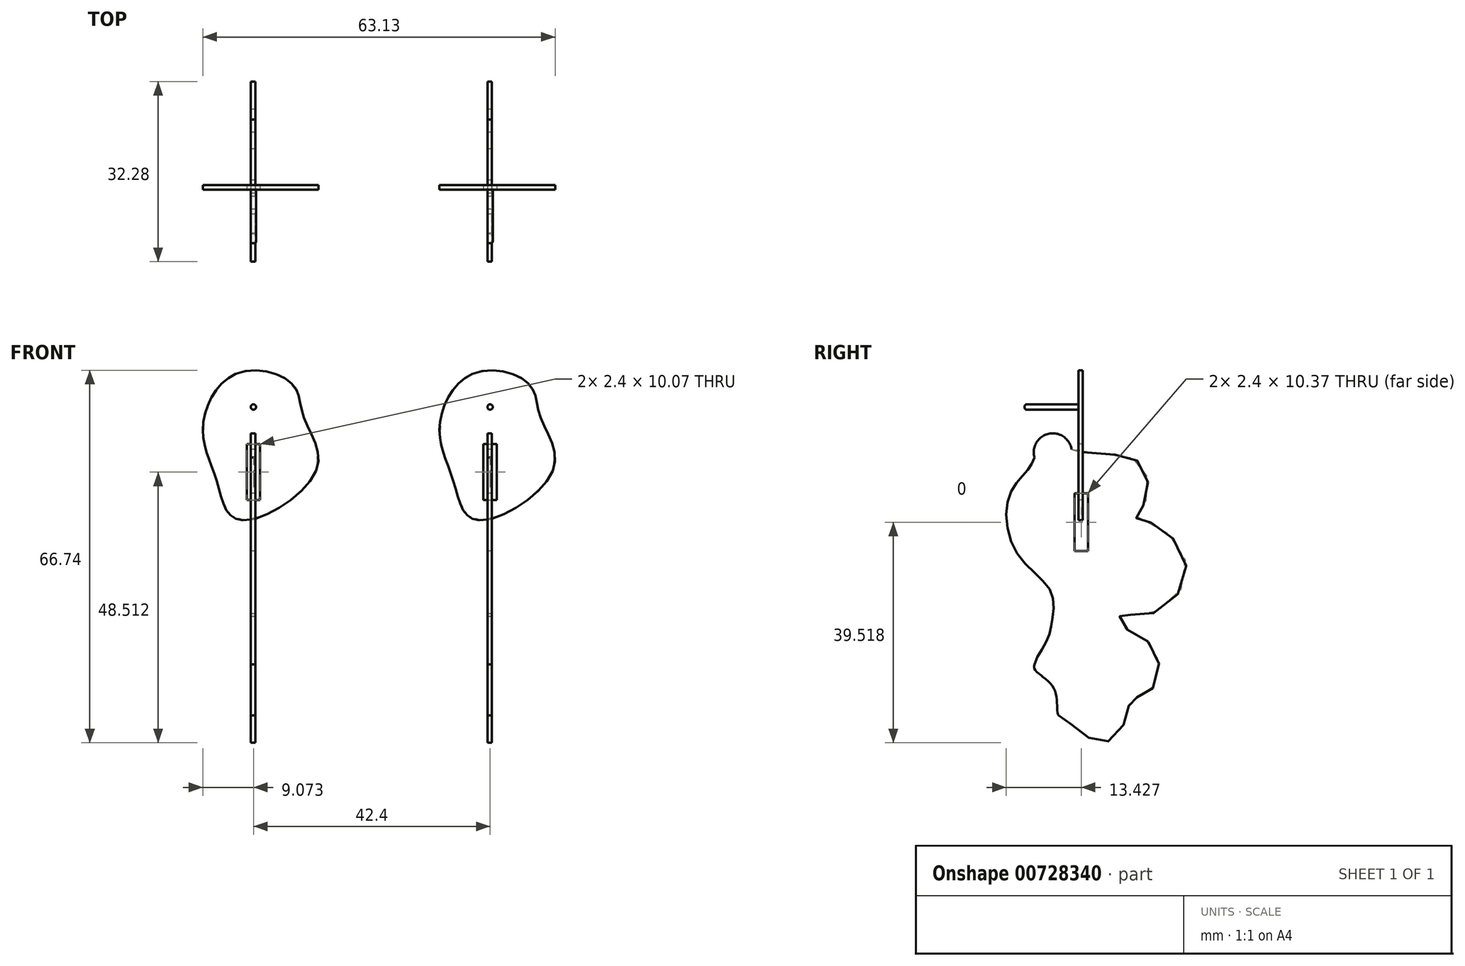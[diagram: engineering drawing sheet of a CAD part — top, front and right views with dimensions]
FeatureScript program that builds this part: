
annotation { "Feature Type Name" : "Feature", "Feature Type Description" : "" }
export const myFeature = defineFeature(function(context is Context, id is Id, definition is map)
    precondition{}
    {
        {
            var Q0;
            Q0=qCreatedBy(makeId("Front.planeOp"),FACE);
            var sketch = newSketch(context, id + "F0", { "sketchPlane" : qUnion([Q0])});
            skFitSpline(sketch, "E0", {"points": [v(-12.68, 26.38) * mm, v(-20.04, 14.2) * mm, v(-17, 2.54) * mm, v(-11.92, -6.34) * mm, v(5.41, 4.9) * mm, v(2.54, 16.74) * mm, v(0, 24.1) * mm, v(-12.68, 26.38) * mm]});
            skSolve(sketch);
        }
        {
            var Q0;
            Q0=makeQuery(id+"F0.imprint","IMPRINT",FACE,{"disambiguationData":[TD([[makeQuery(id+"F0.imprint","IMPRINT",EDGE,{"derivedFrom":sQuery(id+"F0.wireOp",EDGE,"E0")}),1.0]])]});
            extrude(context, id + "F1", {"entities" : qUnion([Q0]), "depth" : 1 * mm, "offsetDistance" : 25.4 * mm});
        }
        {
            var Q0;
            Q0=makeQuery(id+"F1.opExtrude","CAP_FACE",FACE,{"disambiguationData":[OSD([sQuery(id+"F0.wireOp",EDGE,"E0")])],"isStart":false});
            var sketch = newSketch(context, id + "F2", { "sketchPlane" : qUnion([Q0])});
            skLineSegment(sketch, "E1.bottom", {"start": v(-10.2, 10.67) * mm, "end": v(-7.2, 10.67) * mm});
            skLineSegment(sketch, "E1.top", {"start": v(-10.2, -1.92) * mm, "end": v(-7.2, -1.92) * mm});
            skLineSegment(sketch, "E1.left", {"start": v(-10.2, 10.67) * mm, "end": v(-10.2, -1.92) * mm});
            skLineSegment(sketch, "E1.right", {"start": v(-7.2, 10.67) * mm, "end": v(-7.2, -1.92) * mm});
            skSolve(sketch);
        }
        {
            var Q0;
            Q0=makeQuery(id+"F2.imprint","IMPRINT",FACE,{"disambiguationData":[TD([[makeQuery(id+"F2.imprint","IMPRINT",EDGE,{"derivedFrom":sQuery(id+"F2.wireOp",EDGE,"E1.bottom")}),-1.0]])]});
            extrude(context, id + "F3", {"entities" : qUnion([Q0]), "operationType" : NewBodyOperationType.REMOVE, "oppositeDirection" : true, "depth" : 25 * mm, "offsetDistance" : 25 * mm});
        }
        {
            var Q0;
            Q0=makeQuery(id+"F1.opExtrude","CAP_FACE",FACE,{"disambiguationData":[OSD([sQuery(id+"F0.wireOp",EDGE,"E0")])],"isStart":false});
            var sketch = newSketch(context, id + "F4", { "sketchPlane" : qUnion([Q0])});
            skCircle(sketch, "E2", {"center": v(-8.7, 18.96) * mm, "radius": 0.6 * mm});
            skPoint(sketch, "E2.centerSnap0", {"position": v(-8.7, 10.67) * mm});
            skSolve(sketch);
        }
        {
            var Q0;
            Q0=makeQuery(id+"F4.imprint","IMPRINT",FACE,{"disambiguationData":[TD([[makeQuery(id+"F4.imprint","IMPRINT",EDGE,{"derivedFrom":sQuery(id+"F4.wireOp",EDGE,"E2")}),1.0]])]});
            extrude(context, id + "F5", {"entities" : qUnion([Q0]), "operationType" : NewBodyOperationType.ADD, "depth" : 12 * mm, "offsetDistance" : 25 * mm});
        }
        {
            var Q0;
            Q0=makeQuery(id+"F5.opExtrude","CAP_EDGE",EDGE,{"disambiguationData":[OSD([sQuery(id+"F4.wireOp",EDGE,"E2")])],"isStart":false});
            fillet(context, id + "F6", {"entities" : qUnion([Q0]), "radius" : .4 * mm, "tangentPropagation" : true, "allowEdgeOverflow" : false});
        }
        {
            var Q0;
            Q0=qCreatedBy(makeId("Right.planeOp"),FACE);
            var sketch = newSketch(context, id + "F7", { "sketchPlane" : qUnion([Q0])});
            skFitSpline(sketch, "E3", {"points": [v(0.67, 14.67) * mm, v(5.78, 11.07) * mm, v(20.26, 8.72) * mm, v(22.6, 0) * mm, v(20.26, -4.26) * mm, v(24.67, -5.81) * mm, v(31.42, -17.23) * mm, v(21.56, -26.32) * mm, v(16.89, -25.8) * mm, v(17.15, -28.4) * mm, v(24.41, -33.59) * mm, v(23.38, -43.19) * mm, v(19.22, -45) * mm, v(18.18, -48.64) * mm, v(13.25, -54.6) * mm, v(6.25, -50.98) * mm, v(2.91, -48.52) * mm], "startDerivative": vector(-204.35, 44.01) * mm, "endDerivative": vector(-55.54, 25) * mm});
            skArc(sketch, "E4", {"start": v(5.78, 11.07) * mm, "mid": v(0.67, 14.57) * mm, "end": v(-2.52, 9.27) * mm});
            skFitSpline(sketch, "E5", {"points": [v(-2.52, 9.27) * mm, v(-4.52, 5.93) * mm, v(-8.39, 0) * mm, v(-6.24, -12.48) * mm, v(1.01, -20.5) * mm, v(1.49, -27.17) * mm, v(0, -32.28) * mm, v(-2.52, -37.1) * mm], "startDerivative": vector(-11.27, -37.93) * mm, "endDerivative": vector(-6.88, -38.98) * mm});
            skFitSpline(sketch, "E6", {"points": [v(-2.52, -37.1) * mm, v(1.64, -42.13) * mm, v(2.91, -48.52) * mm], "startDerivative": vector(-4.4, -10.49) * mm, "endDerivative": vector(4.35, -4.55) * mm});
            skPoint(sketch, "E7", {"position": v(0.67, 14.57) * mm});
            skSolve(sketch);
        }
        {
            var Q0;
            Q0 = qSketchRegion(id + "F7", true);
            extrude(context, id + "F8", {"entities" : qUnion([Q0]), "depth" : 1 * mm, "offsetDistance" : 25 * mm});
        }
        {
            var Q0;
            Q0=makeQuery(id+"F8.opExtrude","CAP_FACE",FACE,{"disambiguationData":[OSD([sQuery(id+"F7.wireOp",EDGE,"DduFVrHf-Oizk-C7s7-xqRS-AmLVt9ThVnEu"),sQuery(id+"F7.wireOp",EDGE,"E3"),sQuery(id+"F7.wireOp",EDGE,"DQWAIgUf-YkfC-N1zX-nKCW-ZSinzNLoVrHM"),sQuery(id+"F7.wireOp",EDGE,"IZpeJpQK-BhAC-cSWN-AG4q-EBpBSgwZeZnN")])],"isStart":true});
            var sketch = newSketch(context, id + "F9", { "sketchPlane" : qUnion([Q0])});
            skLineSegment(sketch, "E8.bottom", {"start": v(-9.45, 1.22) * mm, "end": v(-6.45, 1.22) * mm});
            skLineSegment(sketch, "E8.top", {"start": v(-9.45, -11.75) * mm, "end": v(-6.45, -11.75) * mm});
            skLineSegment(sketch, "E8.left", {"start": v(-9.45, 1.22) * mm, "end": v(-9.45, -11.75) * mm});
            skLineSegment(sketch, "E8.right", {"start": v(-6.45, 1.22) * mm, "end": v(-6.45, -11.75) * mm});
            skSolve(sketch);
        }
        {
            var Q0;
            Q0 = qSketchRegion(id + "F9", true);
            extrude(context, id + "F10", {"entities" : qUnion([Q0]), "operationType" : NewBodyOperationType.REMOVE, "oppositeDirection" : true, "depth" : 25 * mm, "offsetDistance" : 25 * mm});
        }
        {
            var Q0;
            Q0=makeQuery(id+"F8.opExtrude","SWEPT_BODY",BODY,{"disambiguationData":[OSD([sQuery(id+"F7.wireOp",EDGE,"DduFVrHf-Oizk-C7s7-xqRS-AmLVt9ThVnEu"),sQuery(id+"F7.wireOp",EDGE,"E3"),sQuery(id+"F7.wireOp",EDGE,"DQWAIgUf-YkfC-N1zX-nKCW-ZSinzNLoVrHM"),sQuery(id+"F7.wireOp",EDGE,"IZpeJpQK-BhAC-cSWN-AG4q-EBpBSgwZeZnN")])]});
            transform(context, id + "F11", {"entities" : qUnion([Q0]), "transformType" : TransformType.TRANSLATION_3D, "dx" : -9.3 * mm, "dy" : -8.8 * mm, "dz" : -1.9 * mm, "makeCopy" : false});
        }
        {
            var Q0;
            Q0=makeQuery(id+"F8.opExtrude","SWEPT_BODY",BODY,{"disambiguationData":[OSD([sQuery(id+"F7.wireOp",EDGE,"DduFVrHf-Oizk-C7s7-xqRS-AmLVt9ThVnEu"),sQuery(id+"F7.wireOp",EDGE,"E3"),sQuery(id+"F7.wireOp",EDGE,"DQWAIgUf-YkfC-N1zX-nKCW-ZSinzNLoVrHM"),sQuery(id+"F7.wireOp",EDGE,"IZpeJpQK-BhAC-cSWN-AG4q-EBpBSgwZeZnN")])]});
            transform(context, id + "F12", {"entities" : qUnion([Q0]), "transformType" : TransformType.TRANSLATION_3D, "dx" : 0 * mm, "dy" : 0.5 * mm, "dz" : 0.3 * mm, "makeCopy" : false});
        }
        {
            var Q0;
            Q0=makeQuery(id+"F1.opExtrude","SWEPT_BODY",BODY,{"disambiguationData":[OSD([sQuery(id+"F0.wireOp",EDGE,"E0")])]});
            var Q1;
            Q1=makeQuery(id+"F8.opExtrude","SWEPT_BODY",BODY,{"disambiguationData":[OSD([sQuery(id+"F7.wireOp",EDGE,"DduFVrHf-Oizk-C7s7-xqRS-AmLVt9ThVnEu"),sQuery(id+"F7.wireOp",EDGE,"E3"),sQuery(id+"F7.wireOp",EDGE,"IZpeJpQK-BhAC-cSWN-AG4q-EBpBSgwZeZnN"),sQuery(id+"F7.wireOp",EDGE,"E4")])]});
            var Q2;
            Q2=qCreatedBy(makeId("Origin.pointOp"),VERTEX);
            transform(context, id + "F13", {"entities" : qUnion([Q0, Q1]), "transformType" : TransformType.SCALE_UNIFORMLY, "scale" : .8, "scalePoint" : qUnion([Q2]), "makeCopy" : false});
        }
        {
            var Q0;
            Q0=makeQuery(id+"F8.opExtrude","SWEPT_BODY",BODY,{"disambiguationData":[OSD([sQuery(id+"F7.wireOp",EDGE,"DduFVrHf-Oizk-C7s7-xqRS-AmLVt9ThVnEu"),sQuery(id+"F7.wireOp",EDGE,"E3"),sQuery(id+"F7.wireOp",EDGE,"IZpeJpQK-BhAC-cSWN-AG4q-EBpBSgwZeZnN"),sQuery(id+"F7.wireOp",EDGE,"E4")])]});
            var Q1;
            Q1=makeQuery(id+"F1.opExtrude","SWEPT_BODY",BODY,{"disambiguationData":[OSD([sQuery(id+"F0.wireOp",EDGE,"E0")])]});
            transform(context, id + "F14", {"entities" : qUnion([Q0, Q1]), "transformType" : TransformType.COPY});
        }
        {
            var Q0;
            Q0=makeQuery(id+"F1.opExtrude","SWEPT_BODY",BODY,{"disambiguationData":[OSD([sQuery(id+"F0.wireOp",EDGE,"E0")])]});
            var Q1;
            Q1=makeQuery(id+"F8.opExtrude","SWEPT_BODY",BODY,{"disambiguationData":[OSD([sQuery(id+"F7.wireOp",EDGE,"DduFVrHf-Oizk-C7s7-xqRS-AmLVt9ThVnEu"),sQuery(id+"F7.wireOp",EDGE,"E3"),sQuery(id+"F7.wireOp",EDGE,"IZpeJpQK-BhAC-cSWN-AG4q-EBpBSgwZeZnN"),sQuery(id+"F7.wireOp",EDGE,"E4")])]});
            transform(context, id + "F15", {"entities" : qUnion([Q0, Q1]), "transformType" : TransformType.TRANSLATION_3D, "dx" : 42.4 * mm, "dy" : 0 * mm, "dz" : 0 * mm, "makeCopy" : false});
        }
    });
